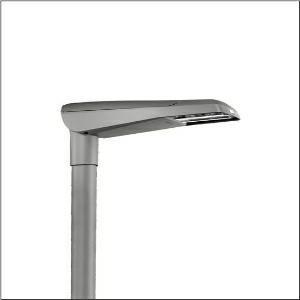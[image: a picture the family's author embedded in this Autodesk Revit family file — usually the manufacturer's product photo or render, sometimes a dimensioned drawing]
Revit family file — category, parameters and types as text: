
# Revit family: streetlight_sl_11_iq_micro___st1_2a_5xc1a21f08ce_ee83
name_source: partatom
category: Lighting Fixtures
units: mm (PartAtom-declared; Revit-internal decimal feet)

## family parameters
Cut with Voids When Loaded = No
Host = Face
Light Source = No
Part Type = Normal
Room Calculation Point = No
Round Connector Dimension = Use Diameter
Shared = No

## types (1)
- --- (1 x LED, 1540 lm, 12.6 W, 2200K)
    Apparent Load = 13 VA
    CIE Flux Codes = 33 71 96 100 100
    Color Rendering = 70
    Color Temperature = 2200K
    Default Elevation = 1800 mm
    Description = Streetlight SL 11 iQ micro, mast luminaire, primary light control with 3 zone facetted reflector, of plastic, silver coated, highly specular, primary optical cover: cover, of PMMA, transparent, light distribution: ST1.2a, light emission: direct distribution, primary light characteristic: asymmetric, installation type: post-top, side-entry, lamps: LED, High Power LED, rated values: 1.540lm | 12,6W | 122,2lm/W (begin service life); end service life: 1.540lm | 12,9W; at 50% lumin. flux: 770lm | 6,8W | 113,2lm/W, colour temperature: 2200K, colour rendering: CRI > 70, light colour: 722, light setting 1 begin service life: 100% | 1.540lm | 12,6W | 122,2lm/W | 2.200K, light setting 1 end service life: 12,9W, further light settings possible, control: Street-Remote, optimised constant luminous flux control (CLO 2.0), Desk-Remote (wireless, voltage-free reading and setting of iQ features in the workshop via application-optimized NFC function/RFID function), Light-Fading, Smart-Wire, Night-Set, Lumen-Switch, Temp-Guard, Auto-Match, with cable H07RN-F 5x 1.5mm², mains connection: 230..240V, AC, 50/60Hz, connection cable pre-assembled, cable length: 5,5m, luminaire housing, of diecast aluminium, powder-coated, Siteco® metallic grey (DB 702S), please order mast flange separately, inclination adjustable without tools: 0°, 5°, 10°, 15° (post-top) | 0°, -5°, -10°, -15° (side-entry), sealing non-destructively replaceable, multi-level sealing system, length: 600mm, width: 174mm, height: 116mm, mast flange for spigot size: 42mm (side-entry): 5XC10008XM4, 60/48mm (side-entry/post-top): 5XC10108XM2, 76/60mm (side-entry/post-top): 5XC10108XM1, equipment: standard, protection rating (complete): IP66, insulation class (complete): insulation class II (safety insulation), certification: CE, ENEC, ENEC+, VDE, impact resistance: IK10, permissible operating ambient temperature for outdoor applications: -25..+50°C, standard-compliant lighting for roads and squares, Environmental Product Declaration (EPD) tested and certified by an independent institute, packaging unit: 1 piece

Light Distribution: ST1.2a
    Height = 116 mm
    Lamp = 1 x LED
    Lamp Light Flux = 1540 lm
    Lamp Power = 12.6 W
    Lamp count = 1
    Length = 600 mm
    Luminous efficacy = 122 lm/W
    Manufacturer = Siteco
    ModVariant = No
    Model = 5XC1A21F08CE
    Number of Poles = 1
    OnlyDefault = Yes
    Power Factor = 1
    Product Name = Streetlight SL 11 iQ micro | ST1.2a
    Product group = mast luminaire | pylon top
    ProductGroupID = 6100
    Protection Class = Protection class II
    Protection Degree = IP 66
    RLX_Detail_Level = 1
    RLX_Emergency_Light_Flux = 0 lm
    RLX_Emergency_Type = 0
    RLX_Emergency_Type_DB = No
    RlxData = <blob elided: 26517 chars, md5=4fd354b2>
    Socket = socket
    Standby Power = 0 W
    System Light Flux = 1540 lm
    System Power = 13 W
    Type Comments = factory setting: luminous flux: 100 % | dim-lin: 254 | 229 mA
    Type Image = l_1006566.jpg
    URL = http://relux.com
    VarID = @adj_017945
    Voltage = 0 V
    Weight = 0.00 kg
    Width = 174 mm

## geometry (parser evidence)
native form markers: Blend x4, Sweep x10
no freeform markers — native parametric forms only
